FCSTD DOCUMENT  (FreeCAD 0.21R38887 (Git))
Label: ЗбіркаПрофілю
License: All rights reserved
LicenseURL: https://en.wikipedia.org/wiki/All_rights_reserved
objects: App::FeaturePython×2, Part::FeaturePython×2, PartDesign::SubShapeBinder×1, PartDesign::LinearPattern×1, PartDesign::Body×1, App::Link×1
note: 6 computed .brp shape members not serialized (recipe doc carries the construction recipe); baked Part::Feature solids carry a one-line shape summary decoded from their .brp
EXTERNAL_REF file=ТаблицаПараметров.FCStd obj=Spreadsheet001
EXTERNAL_REF file=Деталі/8080.FCStd obj=Body

FEATURE [App::FeaturePython] Constraints  # WARN: FeaturePython — macro-defined, semantics opaque (R4)
  TreeRank = 37
  _LinkVersion = 1
  _Version = 1
FEATURE [App::FeaturePython] Elements  # WARN: FeaturePython — macro-defined, semantics opaque (R4)
  TreeRank = 38
  _LinkVersion = 1
FEATURE [PartDesign::SubShapeBinder] BaseFeature001  label="BaseFeature001(Профиль80х80)"
  BindCopyOnChange = 0
  BindMode = 0
  ClaimChildren = false
  Context = -> Assembly [Parts.Body.BaseFeature001.]
  EdgeTolerance = 1e-06
  FillStyle = 0
  Fuse = true
  InvalidShape = false
  MakeFace = true
  MergeEdges = true
  OffsetFill = false
  OffsetIntersection = false
  OffsetJoinType = 0
  OffsetOpenResult = false
  Outline = false
  PartialLoad = false
  Relative = true
  SplitEdges = false
  TightBound = false
  TreeRank = 51
  ValidateShape = false
  _Version = 8
FEATURE [PartDesign::LinearPattern] LinearPattern
  AddSubType = 0
  BaseFeature = -> BaseFeature001
  CopyShape = false
  Direction = -> X_Axis
  InvalidShape = false
  Length = 720
  NewSolid = false
  Occurrences = 10
  OriginalSubs = -> [BaseFeature001]
  Originals = -> [BaseFeature001]
  ParallelTransform = true
  SubTransform = true
  Suppress = false
  TreeRank = 52
  ValidateShape = true
  _Version = 3
  expr: Length = ТаблицаПараметров#<<ТаблСтанина>>.GlubinaStaninu - ТаблицаПараметров#<<ТаблСтанина>>.RazmerProfilja
  expr: Occurrences = ТаблицаПараметров#<<ТаблСтанина>>.NumberProfileBody
FEATURE [PartDesign::Body] Body
  AutoGroupSolids = false
  BaseFeature = -> BaseFeature001
  ClaimAllChildren = false
  ExportMode = 0
  Group = -> [BaseFeature001,LinearPattern]
  InvalidShape = false
  Origin = -> Origin
  Tip = -> LinearPattern
  TreeRank = 50
  ValidateShape = false
  _ExportChildren = -> [BaseFeature001,LinearPattern]
  _GroupVersion = 1
FEATURE [Part::FeaturePython] Parts  # WARN: FeaturePython — macro-defined, semantics opaque (R4)
  Group = -> [Body]
  GroupMode = 0
  InvalidShape = false
  TreeRank = 39
  ValidateShape = false
  _LinkVersion = 1
FEATURE [Part::FeaturePython] Assembly  label="МасивПрофілю"  # WARN: FeaturePython — macro-defined, semantics opaque (R4)
  AutoRelax = true
  BuildShape = 0
  Freeze = false
  Group = -> [Constraints,Elements,Parts]
  InvalidShape = false
  TreeRank = 36
  ValidateShape = false
  Verbose = false
  _LinkVersion = 1
  _SolverType = 1
  _Version = 1
FEATURE [App::Link] Link001  label="Профиль80х80"
  AutoLinkLabel = true
  AutoPlacement = true
  LinkedObject = -> <external Деталі/8080.FCStd>#Body
  SyncGroupVisibility = false
  TreeRank = 53
  _LinkVersion = 1
